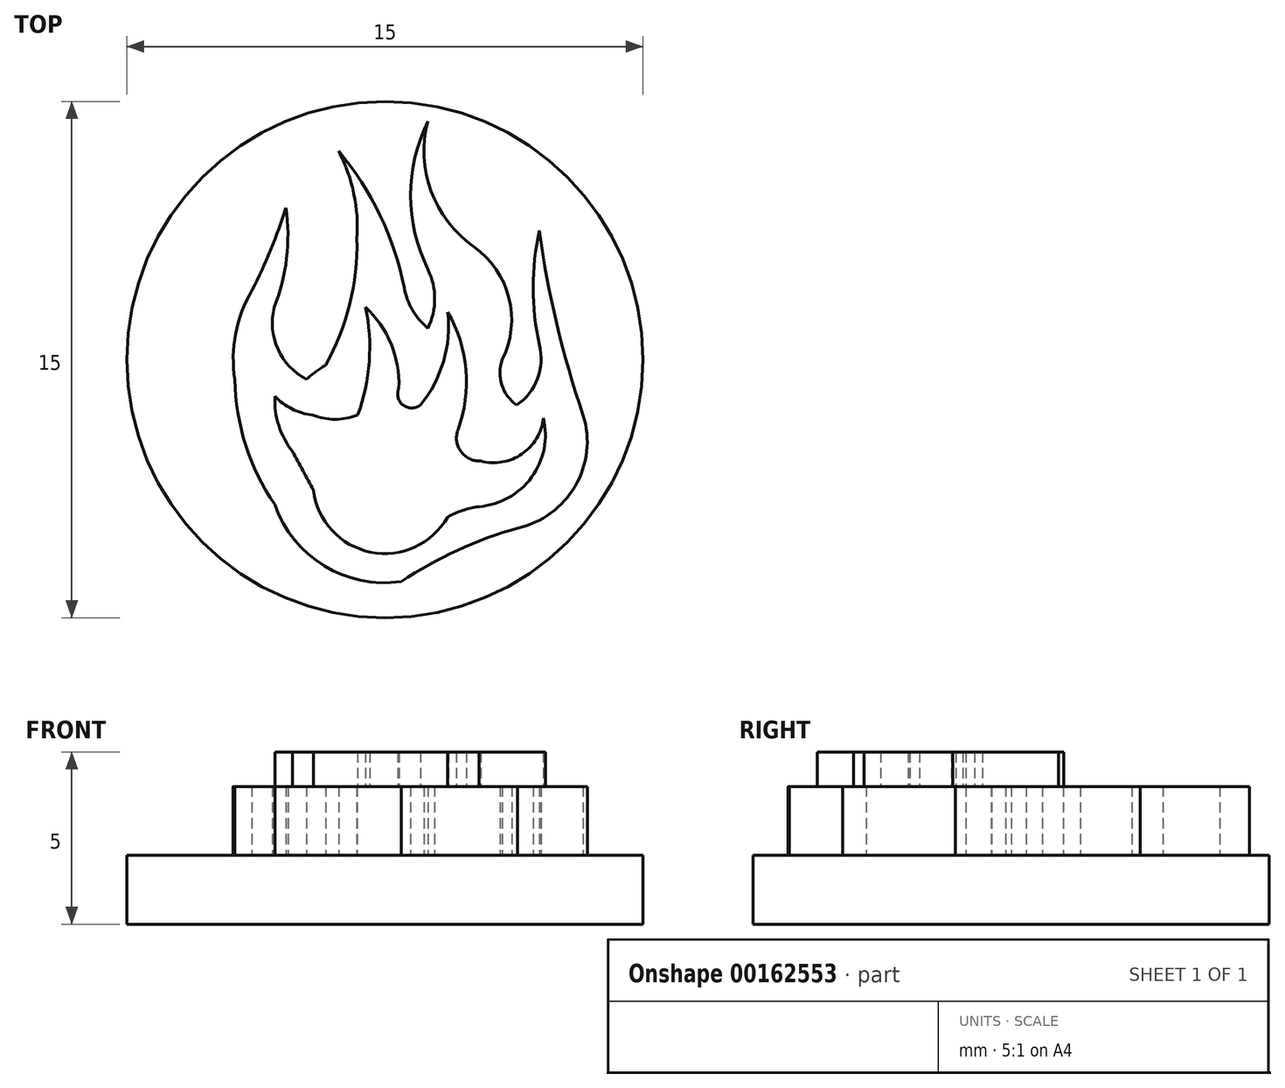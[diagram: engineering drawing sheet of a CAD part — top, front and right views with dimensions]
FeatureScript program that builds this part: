
annotation { "Feature Type Name" : "Feature", "Feature Type Description" : "" }
export const myFeature = defineFeature(function(context is Context, id is Id, definition is map)
    precondition{}
    {
        {
            var Q0;
            Q0=qCreatedBy(makeId("Top.planeOp"),FACE);
            var sketch = newSketch(context, id + "F0", { "sketchPlane" : qUnion([Q0])});
            skCircle(sketch, "E0", {"center": v(0, 0) * mm, "radius": 7.5 * mm});
            skSolve(sketch);
        }
        {
            var Q0;
            Q0 = qSketchRegion(id + "F0", true);
            extrude(context, id + "F1", {"entities" : qUnion([Q0]), "depth" : 2 * mm});
        }
        {
            var Q0;
            Q0=makeQuery(id+"F1.opExtrude","CAP_FACE",FACE,{"disambiguationData":[OSD([sQuery(id+"F0.wireOp",EDGE,"E0")])],"isStart":false});
            var sketch = newSketch(context, id + "F2", { "sketchPlane" : qUnion([Q0])});
            skArc(sketch, "E1", {"start": v(-3.2, -4.22) * mm, "mid": v(-1.76, -5.99) * mm, "end": v(0.47, -6.45) * mm});
            skArc(sketch, "E2", {"start": v(-1.72, -0.16) * mm, "mid": v(-1.02, 1.61) * mm, "end": v(-0.81, 3.5) * mm});
            skArc(sketch, "E3", {"start": v(-0.81, 3.5) * mm, "mid": v(-0.9, 4.82) * mm, "end": v(-1.35, 6.06) * mm});
            skArc(sketch, "E4", {"start": v(0.56, 2.08) * mm, "mid": v(-0.14, 4.2) * mm, "end": v(-1.35, 6.06) * mm});
            skArc(sketch, "E5", {"start": v(0.56, 2.08) * mm, "mid": v(0.8, 1.44) * mm, "end": v(1.25, 0.9) * mm});
            skArc(sketch, "E6", {"start": v(1.25, 0.9) * mm, "mid": v(1.45, 1.77) * mm, "end": v(1.25, 2.62) * mm});
            skArc(sketch, "E7", {"start": v(1.25, 6.92) * mm, "mid": v(0.75, 4.77) * mm, "end": v(1.25, 2.62) * mm});
            skArc(sketch, "E8", {"start": v(1.25, 6.92) * mm, "mid": v(1.34, 4.9) * mm, "end": v(2.58, 3.28) * mm});
            skArc(sketch, "E9", {"start": v(3.4, 0) * mm, "mid": v(3.6, 1.8) * mm, "end": v(2.58, 3.28) * mm});
            skArc(sketch, "E10", {"start": v(3.4, 0) * mm, "mid": v(3.4, -0.73) * mm, "end": v(3.83, -1.32) * mm});
            skArc(sketch, "E11", {"start": v(3.83, -1.32) * mm, "mid": v(4.43, -0.55) * mm, "end": v(4.48, 0.43) * mm});
            skArc(sketch, "E12", {"start": v(4.48, 3.75) * mm, "mid": v(4.3, 2.09) * mm, "end": v(4.48, 0.43) * mm});
            skArc(sketch, "E13", {"start": v(4.48, 3.75) * mm, "mid": v(5, 1.03) * mm, "end": v(5.76, -1.62) * mm});
            skArc(sketch, "E14", {"start": v(3.86, -4.9) * mm, "mid": v(5.53, -3.67) * mm, "end": v(5.76, -1.62) * mm});
            skArc(sketch, "E15", {"start": v(3.86, -4.9) * mm, "mid": v(2.1, -5.54) * mm, "end": v(0.47, -6.45) * mm});
            skArc(sketch, "E16", {"start": v(-3.22, 1.51) * mm, "mid": v(-3.11, 0.3) * mm, "end": v(-2.28, -0.57) * mm});
            skArc(sketch, "E17", {"start": v(-3.22, 1.51) * mm, "mid": v(-2.86, 2.94) * mm, "end": v(-2.87, 4.4) * mm});
            skArc(sketch, "E18", {"start": v(-3.86, 2) * mm, "mid": v(-3.32, 3.2) * mm, "end": v(-2.87, 4.4) * mm});
            skArc(sketch, "E19", {"start": v(-3.86, 2) * mm, "mid": v(-4.34, 0.76) * mm, "end": v(-4.36, -0.58) * mm});
            skArc(sketch, "E20", {"start": v(-4.36, -0.58) * mm, "mid": v(-4.05, -2.49) * mm, "end": v(-3.2, -4.22) * mm});
            skArc(sketch, "E21.trimOffspring", {"start": v(-1.72, -0.16) * mm, "mid": v(-2, -0.35) * mm, "end": v(-2.28, -0.57) * mm});
            skSolve(sketch);
        }
        {
            var Q0;
            Q0 = qSketchRegion(id + "F2", true);
            extrude(context, id + "F3", {"entities" : qUnion([Q0]), "operationType" : NewBodyOperationType.ADD, "depth" : 2 * mm});
        }
        {
            var Q0;
            Q0=makeQuery(id+"F3.opExtrude","CAP_FACE",FACE,{"disambiguationData":[OSD([sQuery(id+"F2.wireOp",EDGE,"E1"),sQuery(id+"F2.wireOp",EDGE,"E2"),sQuery(id+"F2.wireOp",EDGE,"E3"),sQuery(id+"F2.wireOp",EDGE,"E4"),sQuery(id+"F2.wireOp",EDGE,"E5"),sQuery(id+"F2.wireOp",EDGE,"E6"),sQuery(id+"F2.wireOp",EDGE,"E7"),sQuery(id+"F2.wireOp",EDGE,"E8"),sQuery(id+"F2.wireOp",EDGE,"E9"),sQuery(id+"F2.wireOp",EDGE,"E10"),sQuery(id+"F2.wireOp",EDGE,"E11"),sQuery(id+"F2.wireOp",EDGE,"E12"),sQuery(id+"F2.wireOp",EDGE,"E13"),sQuery(id+"F2.wireOp",EDGE,"E14"),sQuery(id+"F2.wireOp",EDGE,"E15"),sQuery(id+"F2.wireOp",EDGE,"E16"),sQuery(id+"F2.wireOp",EDGE,"E17"),sQuery(id+"F2.wireOp",EDGE,"E18"),sQuery(id+"F2.wireOp",EDGE,"E19"),sQuery(id+"F2.wireOp",EDGE,"E20"),sQuery(id+"F2.wireOp",EDGE,"E21.trimOffspring")])],"isStart":false});
            var sketch = newSketch(context, id + "F4", { "sketchPlane" : qUnion([Q0])});
            skArc(sketch, "E22", {"start": v(-2.08, -3.8) * mm, "mid": v(-0.41, -5.6) * mm, "end": v(1.82, -4.58) * mm});
            skArc(sketch, "E23", {"start": v(-2.68, -2.67) * mm, "mid": v(-2.38, -3.23) * mm, "end": v(-2.08, -3.8) * mm});
            skArc(sketch, "E24", {"start": v(-3.2, -1.06) * mm, "mid": v(-3.09, -1.91) * mm, "end": v(-2.68, -2.67) * mm});
            skArc(sketch, "E25", {"start": v(-3.2, -1.06) * mm, "mid": v(-2.7, -1.43) * mm, "end": v(-2.1, -1.6) * mm});
            skArc(sketch, "E26", {"start": v(-2.1, -1.6) * mm, "mid": v(-1.45, -1.73) * mm, "end": v(-0.79, -1.6) * mm});
            skArc(sketch, "E27", {"start": v(-0.79, -1.6) * mm, "mid": v(-0.46, -0.06) * mm, "end": v(-0.56, 1.53) * mm});
            skArc(sketch, "E28", {"start": v(0.4, -0.83) * mm, "mid": v(0.18, 0.46) * mm, "end": v(-0.56, 1.53) * mm});
            skArc(sketch, "E29", {"start": v(0.4, -0.83) * mm, "mid": v(0.53, -1.32) * mm, "end": v(1.04, -1.31) * mm});
            skArc(sketch, "E30", {"start": v(1.04, -1.31) * mm, "mid": v(1.7, -0.05) * mm, "end": v(1.82, 1.38) * mm});
            skArc(sketch, "E31", {"start": v(2.12, -2.04) * mm, "mid": v(2.35, -0.3) * mm, "end": v(1.82, 1.38) * mm});
            skArc(sketch, "E32", {"start": v(2.12, -2.04) * mm, "mid": v(2.2, -2.67) * mm, "end": v(2.79, -2.95) * mm});
            skArc(sketch, "E33", {"start": v(2.79, -2.95) * mm, "mid": v(3.98, -2.74) * mm, "end": v(4.6, -1.7) * mm});
            skArc(sketch, "E34", {"start": v(2.73, -4.27) * mm, "mid": v(4.26, -3.42) * mm, "end": v(4.6, -1.7) * mm});
            skArc(sketch, "E35", {"start": v(2.73, -4.27) * mm, "mid": v(2.26, -4.38) * mm, "end": v(1.82, -4.58) * mm});
            skSolve(sketch);
        }
        {
            var Q0;
            Q0 = qSketchRegion(id + "F4", true);
            extrude(context, id + "F5", {"entities" : qUnion([Q0]), "operationType" : NewBodyOperationType.ADD, "depth" : 1 * mm});
        }
    });
